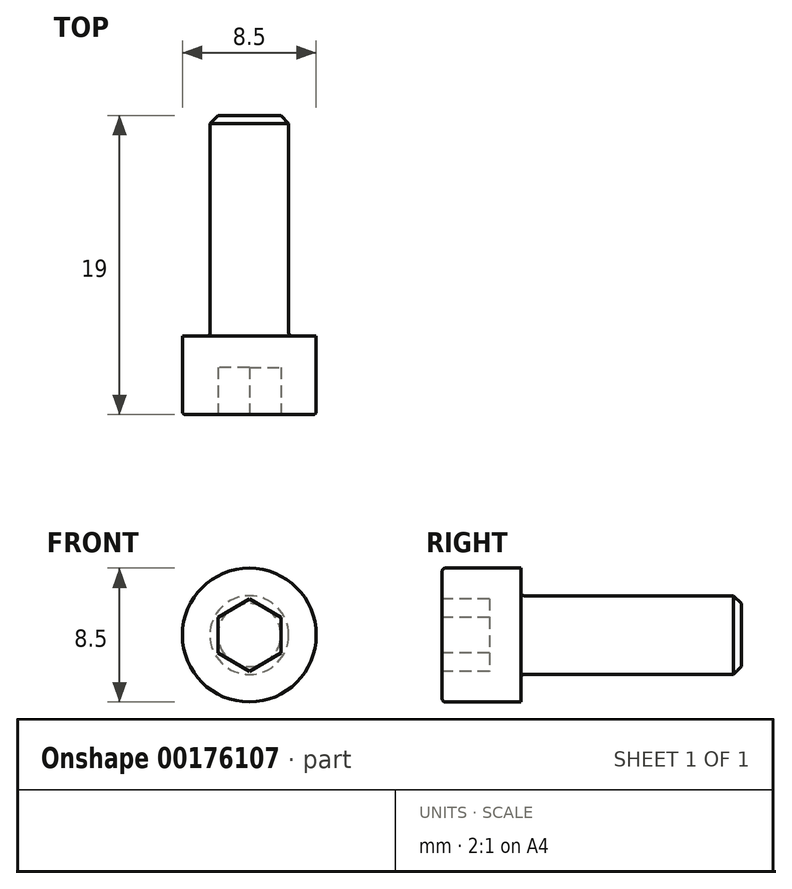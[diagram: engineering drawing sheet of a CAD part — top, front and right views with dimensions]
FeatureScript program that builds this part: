
annotation { "Feature Type Name" : "Feature", "Feature Type Description" : "" }
export const myFeature = defineFeature(function(context is Context, id is Id, definition is map)
    precondition{}
    {
        {
            var Q0;
            Q0=qCreatedBy(makeId("Right.planeOp"),FACE);
            var sketch = newSketch(context, id + "F0", { "sketchPlane" : qUnion([Q0])});
            skLineSegment(sketch, "E0", {"start": v(0, 0) * mm, "end": v(0, 4.25) * mm});
            skLineSegment(sketch, "E1", {"start": v(0, 4.25) * mm, "end": v(5, 4.25) * mm});
            skLineSegment(sketch, "E2", {"start": v(5, 4.25) * mm, "end": v(5, 2.5) * mm});
            skLineSegment(sketch, "E3", {"start": v(5, 2.5) * mm, "end": v(19, 2.5) * mm});
            skLineSegment(sketch, "E4", {"start": v(19, 2.5) * mm, "end": v(19, 0) * mm});
            skLineSegment(sketch, "E5", {"start": v(19, 0) * mm, "end": v(0, 0) * mm});
            skSolve(sketch);
        }
        {
            var Q0;
            Q0 = qSketchRegion(id + "F0", true);
            var Q1;
            Q1=sQuery(id+"F0.wireOp",EDGE,"E5");
            revolve(context, id + "F1", {"entities" : qUnion([Q0]), "axis" : qUnion([Q1]), "revolveType" : RevolveType.FULL});
        }
        {
            var Q0;
            Q0=makeQuery(id+"F1.opRevolve","SWEPT_EDGE",EDGE,{"disambiguationData":[OSD([sQuery(id+"F0.wireOp",EDGE,"E3"),sQuery(id+"F0.wireOp",EDGE,"E4")])]});
            chamfer(context, id + "F2", {"entities" : qUnion([Q0]), "width" : 0.5 * mm, "tangentPropagation" : true});
        }
        {
            var Q0;
            Q0=makeQuery(id+"F1.opRevolve","SWEPT_EDGE",EDGE,{"disambiguationData":[OSD([sQuery(id+"F0.wireOp",EDGE,"E2"),sQuery(id+"F0.wireOp",EDGE,"E3")])]});
            var Q1;
            Q1=makeQuery(id+"F1.opRevolve","SWEPT_EDGE",EDGE,{"disambiguationData":[OSD([sQuery(id+"F0.wireOp",EDGE,"E0"),sQuery(id+"F0.wireOp",EDGE,"E1")])]});
            fillet(context, id + "F3", {"entities" : qUnion([Q0, Q1]), "radius" : 0.2 * mm, "tangentPropagation" : true, "allowEdgeOverflow" : false});
        }
        {
            var Q0;
            Q0=makeQuery(id+"F1.opRevolve","SWEPT_FACE",FACE,{"disambiguationData":[OSD([sQuery(id+"F0.wireOp",EDGE,"E0")])]});
            var sketch = newSketch(context, id + "F4", { "sketchPlane" : qUnion([Q0])});
            skCircle(sketch, "E6", {"center": v(0, 0) * mm, "radius": 2.3 * mm});
            skLineSegment(sketch, "E7", {"start": v(0, 2.3) * mm, "end": v(-2, 1.14) * mm});
            skLineSegment(sketch, "E8", {"start": v(-2, 1.14) * mm, "end": v(-2, -1.14) * mm});
            skLineSegment(sketch, "E9", {"start": v(-2, -1.14) * mm, "end": v(0, -2.3) * mm});
            skLineSegment(sketch, "E10.MirrorCS", {"start": v(0, 2.3) * mm, "end": v(2, 1.14) * mm});
            skLineSegment(sketch, "E11.MirrorCS", {"start": v(2, 1.14) * mm, "end": v(2, -1.14) * mm});
            skLineSegment(sketch, "E12.MirrorCS", {"start": v(2, -1.14) * mm, "end": v(0, -2.3) * mm});
            skSolve(sketch);
        }
        {
            var Q0;
            Q0=makeQuery(id+"F4.imprint","IMPRINT",FACE,{"disambiguationData":[TD([[makeQuery(id+"F4.imprint","IMPRINT",EDGE,{"derivedFrom":sQuery(id+"F4.wireOp",EDGE,"E7")}),1.0]])]});
            extrude(context, id + "F5", {"entities" : qUnion([Q0]), "operationType" : NewBodyOperationType.REMOVE, "oppositeDirection" : true, "depth" : 3 * mm});
        }
    });
